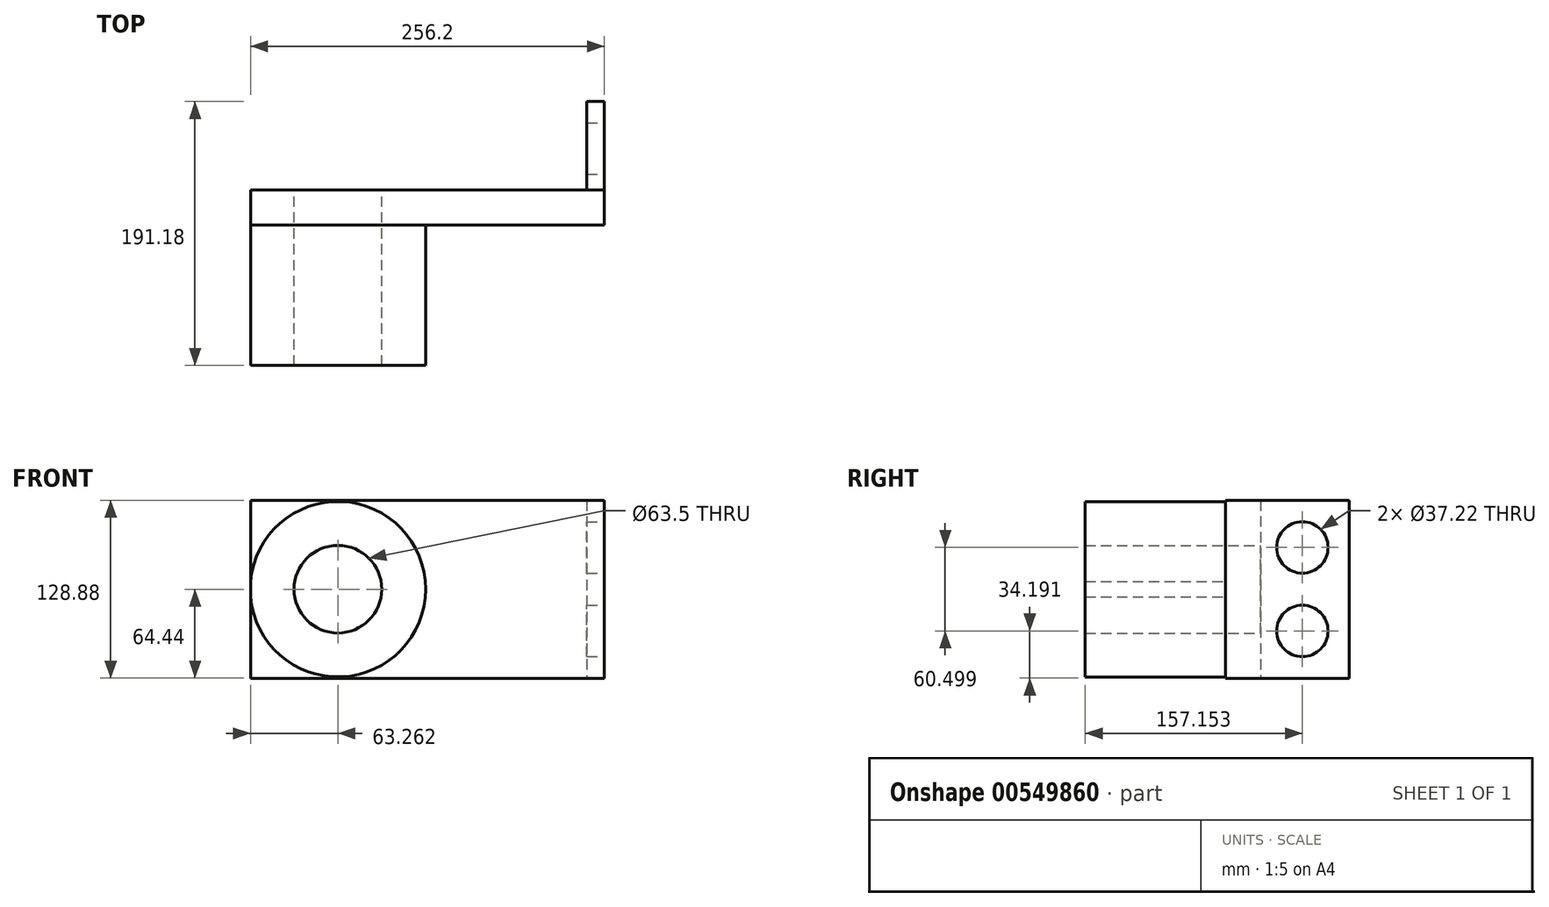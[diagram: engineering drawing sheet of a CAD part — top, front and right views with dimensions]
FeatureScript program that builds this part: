
annotation { "Feature Type Name" : "Feature", "Feature Type Description" : "" }
export const myFeature = defineFeature(function(context is Context, id is Id, definition is map)
    precondition{}
    {
        {
            var Q0;
            Q0=qCreatedBy(makeId("Front.planeOp"),FACE);
            var sketch = newSketch(context, id + "F0", { "sketchPlane" : qUnion([Q0])});
            skLineSegment(sketch, "E0.bottom", {"start": v(-128.1, 64.44) * mm, "end": v(128.1, 64.44) * mm});
            skLineSegment(sketch, "E0.top", {"start": v(-128.1, -64.44) * mm, "end": v(128.1, -64.44) * mm});
            skLineSegment(sketch, "E0.left", {"start": v(-128.1, 64.44) * mm, "end": v(-128.1, -64.44) * mm});
            skLineSegment(sketch, "E0.right", {"start": v(128.1, 64.44) * mm, "end": v(128.1, -64.44) * mm});
            skPoint(sketch, "E0.middle", {"position": v(0, 0) * mm});
            skCircle(sketch, "E1", {"center": v(-64.84, 0) * mm, "radius": 63.5 * mm});
            skCircle(sketch, "E2", {"center": v(-64.84, 0) * mm, "radius": 31.75 * mm});
            skSolve(sketch);
        }
        {
            var Q0;
            Q0=makeQuery(id+"F0.imprint","IMPRINT",FACE,{"disambiguationData":[TD([[makeQuery(id+"F0.imprint","IMPRINT",EDGE,{"derivedFrom":sQuery(id+"F0.wireOp",EDGE,"E2")}),-1.0]])]});
            var Q1;
            {var subQ4=sQuery(id+"F0.wireOp",EDGE,"E0.bottom");Q1=makeQuery(id+"F0.imprint","IMPRINT",FACE,{"disambiguationData":[TD([[makeQuery(id+"F0.imprint","IMPRINT",EDGE,{"derivedFrom":subQ4}),-1.0]])]});}
            extrude(context, id + "F1", {"entities" : qUnion([Q0, Q1]), "depth" : 25.4 * mm, "offsetDistance" : 25.4 * mm});
        }
        {
            var Q0;
            Q0=makeQuery(id+"F0.imprint","IMPRINT",FACE,{"disambiguationData":[TD([[makeQuery(id+"F0.imprint","IMPRINT",EDGE,{"derivedFrom":sQuery(id+"F0.wireOp",EDGE,"E2")}),-1.0]])]});
            extrude(context, id + "F2", {"entities" : qUnion([Q0]), "operationType" : NewBodyOperationType.ADD, "depth" : 127 * mm, "offsetDistance" : 25.4 * mm});
        }
        {
            var Q0;
            Q0=makeQuery(id+"F1.opExtrude","SWEPT_FACE",FACE,{"disambiguationData":[OSD([sQuery(id+"F0.wireOp",EDGE,"E0.right")])]});
            var sketch = newSketch(context, id + "F3", { "sketchPlane" : qUnion([Q0])});
            skLineSegment(sketch, "E3.bottom", {"start": v(-25.4, -64.44) * mm, "end": v(64.18, -64.44) * mm});
            skLineSegment(sketch, "E3.top", {"start": v(-25.4, 64.28) * mm, "end": v(64.18, 64.28) * mm});
            skLineSegment(sketch, "E3.left", {"start": v(-25.4, -64.44) * mm, "end": v(-25.4, 64.28) * mm});
            skLineSegment(sketch, "E3.right", {"start": v(64.18, -64.44) * mm, "end": v(64.18, 64.28) * mm});
            skCircle(sketch, "E4", {"center": v(30.15, -30.25) * mm, "radius": 18.6 * mm});
            skLineSegment(sketch, "E5", {"start": v(0, 0) * mm, "end": v(64.18, 0) * mm, "construction": true});
            skCircle(sketch, "E6.MirrorC", {"center": v(30.15, 30.25) * mm, "radius": 18.6 * mm});
            skSolve(sketch);
        }
        {
            var Q0;
            {var subQ0=sQuery(id+"F3.wireOp",EDGE,"E3.right");Q0=makeQuery(id+"F3.imprint","IMPRINT",FACE,{"disambiguationData":[TD([[makeQuery(id+"F3.imprint","IMPRINT",EDGE,{"derivedFrom":subQ0}),1.0]])]});}
            extrude(context, id + "F4", {"entities" : qUnion([Q0]), "operationType" : NewBodyOperationType.ADD, "oppositeDirection" : true, "depth" : 12.7 * mm, "offsetDistance" : 25.4 * mm});
        }
    });
